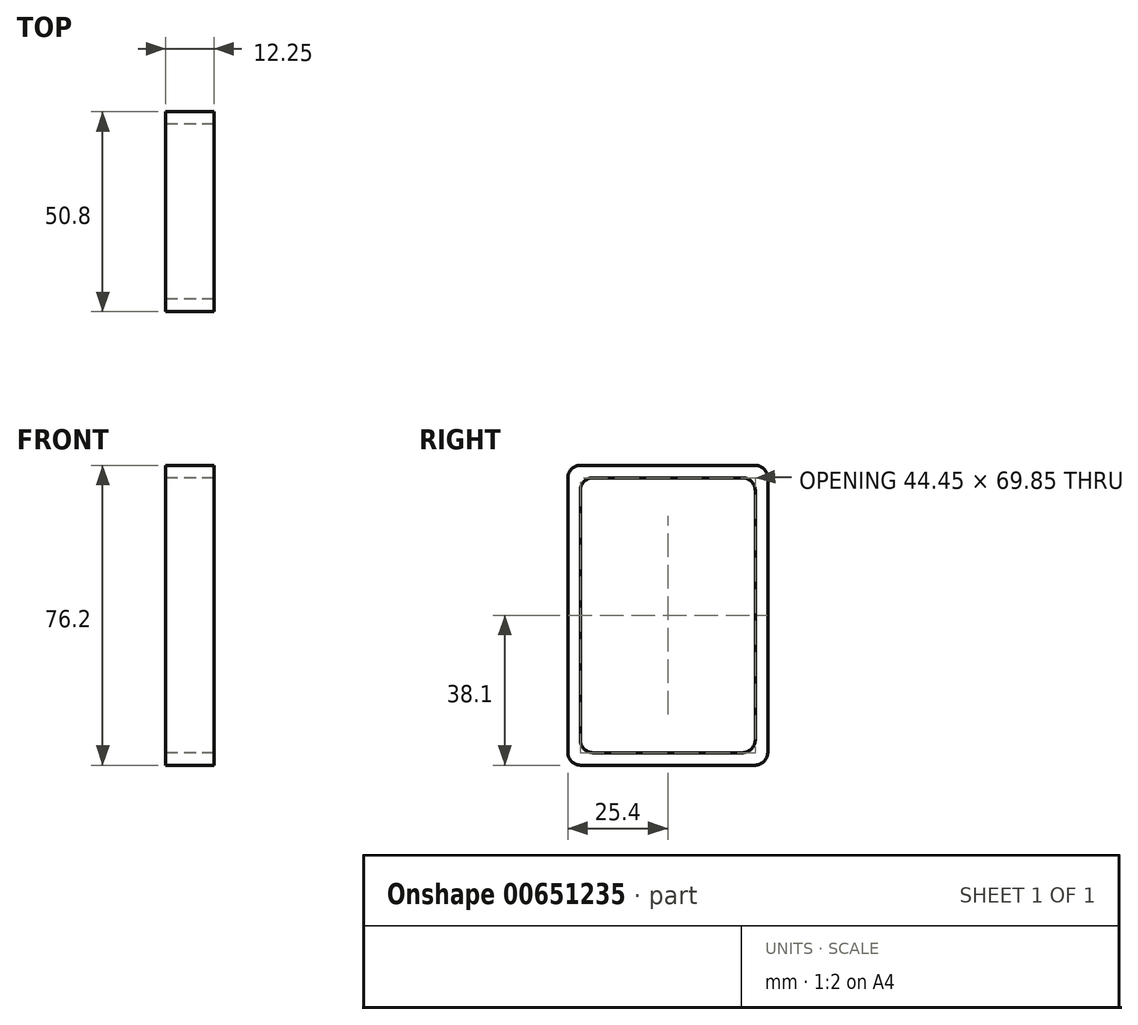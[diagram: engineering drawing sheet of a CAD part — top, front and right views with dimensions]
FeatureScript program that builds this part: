
annotation { "Feature Type Name" : "Feature", "Feature Type Description" : "" }
export const myFeature = defineFeature(function(context is Context, id is Id, definition is map)
    precondition{}
    {
        {
            var Q0;
            Q0=qCreatedBy(makeId("Right.planeOp"),FACE);
            var sketch = newSketch(context, id + "F0", { "sketchPlane" : qUnion([Q0])});
            skLineSegment(sketch, "E0.bottom", {"start": v(25.4, -38.1) * mm, "end": v(-25.4, -38.1) * mm});
            skLineSegment(sketch, "E0.top", {"start": v(25.4, 38.1) * mm, "end": v(-25.4, 38.1) * mm});
            skLineSegment(sketch, "E0.left", {"start": v(25.4, -38.1) * mm, "end": v(25.4, 38.1) * mm});
            skLineSegment(sketch, "E0.right", {"start": v(-25.4, -38.1) * mm, "end": v(-25.4, 38.1) * mm});
            skPoint(sketch, "E0.middle", {"position": v(0, 0) * mm});
            skLineSegment(sketch, "E1.bottom", {"start": v(22.22, -34.92) * mm, "end": v(-22.23, -34.93) * mm});
            skLineSegment(sketch, "E1.top", {"start": v(22.23, 34.93) * mm, "end": v(-22.23, 34.93) * mm});
            skLineSegment(sketch, "E1.left", {"start": v(22.23, -34.92) * mm, "end": v(22.23, 34.93) * mm});
            skLineSegment(sketch, "E1.right", {"start": v(-22.23, -34.93) * mm, "end": v(-22.22, 34.93) * mm});
            skSolve(sketch);
        }
        {
            assignVariable(context, id + "F1", {"name" : "Length", "anyValue" : 12.25});
        }
        {
            var Q0;
            Q0=makeQuery(id+"F0.imprint","IMPRINT",FACE,{"disambiguationData":[TD([[makeQuery(id+"F0.imprint","IMPRINT",EDGE,{"derivedFrom":sQuery(id+"F0.wireOp",EDGE,"E0.bottom")}),-1.0]])]});
            extrude(context, id + "F2", {"entities" : qUnion([Q0]), "depth" : (getVariable(context, 'Length')) * mm, "offsetDistance" : 25.4 * mm});
        }
        {
            var Q0;
            Q0=makeQuery(id+"F2.opExtrude","SWEPT_EDGE",EDGE,{"disambiguationData":[OSD([sQuery(id+"F0.wireOp",EDGE,"E0.top"),sQuery(id+"F0.wireOp",EDGE,"E0.right")])]});
            var Q1;
            Q1=makeQuery(id+"F2.opExtrude","SWEPT_EDGE",EDGE,{"disambiguationData":[OSD([sQuery(id+"F0.wireOp",EDGE,"E1.top"),sQuery(id+"F0.wireOp",EDGE,"E1.right")])]});
            var Q2;
            Q2=makeQuery(id+"F2.opExtrude","SWEPT_EDGE",EDGE,{"disambiguationData":[OSD([sQuery(id+"F0.wireOp",EDGE,"E1.top"),sQuery(id+"F0.wireOp",EDGE,"E1.left")])]});
            var Q3;
            Q3=makeQuery(id+"F2.opExtrude","SWEPT_EDGE",EDGE,{"disambiguationData":[OSD([sQuery(id+"F0.wireOp",EDGE,"E0.top"),sQuery(id+"F0.wireOp",EDGE,"E0.left")])]});
            var Q4;
            Q4=makeQuery(id+"F2.opExtrude","SWEPT_EDGE",EDGE,{"disambiguationData":[OSD([sQuery(id+"F0.wireOp",EDGE,"E0.bottom"),sQuery(id+"F0.wireOp",EDGE,"E0.left")])]});
            var Q5;
            Q5=makeQuery(id+"F2.opExtrude","SWEPT_EDGE",EDGE,{"disambiguationData":[OSD([sQuery(id+"F0.wireOp",EDGE,"E0.bottom"),sQuery(id+"F0.wireOp",EDGE,"E0.right")])]});
            var Q6;
            Q6=makeQuery(id+"F2.opExtrude","SWEPT_EDGE",EDGE,{"disambiguationData":[OSD([sQuery(id+"F0.wireOp",EDGE,"E1.bottom"),sQuery(id+"F0.wireOp",EDGE,"E1.left")])]});
            var Q7;
            Q7=makeQuery(id+"F2.opExtrude","SWEPT_EDGE",EDGE,{"disambiguationData":[OSD([sQuery(id+"F0.wireOp",EDGE,"E1.bottom"),sQuery(id+"F0.wireOp",EDGE,"E1.right")])]});
            fillet(context, id + "F3", {"entities" : qUnion([Q0, Q1, Q2, Q3, Q4, Q5, Q6, Q7]), "radius" : 3.17 * mm, "tangentPropagation" : true, "allowEdgeOverflow" : false});
        }
        {
            var Q0;
            Q0=makeQuery(id+"F2.opExtrude","SWEPT_FACE",FACE,{"disambiguationData":[OSD([sQuery(id+"F0.wireOp",EDGE,"E0.right")])]});
            var sketch = newSketch(context, id + "F4", { "sketchPlane" : qUnion([Q0])});
            skLineSegment(sketch, "E2", {"start": v(155.58, 0) * mm, "end": v(53.98, 0) * mm});
            skPoint(sketch, "E3.middle", {"position": v(53.98, 0) * mm});
            skCircle(sketch, "E4", {"center": v(69.98, 15) * mm, "radius": 3 * mm});
            skCircle(sketch, "E5", {"center": v(37.98, 15) * mm, "radius": 3 * mm});
            skCircle(sketch, "E6", {"center": v(69.98, -15) * mm, "radius": 3 * mm});
            skCircle(sketch, "E7", {"center": v(37.98, -15) * mm, "radius": 3 * mm});
            skCircle(sketch, "E8.MirrorC", {"center": v(241.18, 15) * mm, "radius": 3 * mm});
            skCircle(sketch, "E9.MirrorC", {"center": v(273.18, 15) * mm, "radius": 3 * mm});
            skCircle(sketch, "E10.MirrorC", {"center": v(273.18, -15) * mm, "radius": 3 * mm});
            skCircle(sketch, "E11.MirrorC", {"center": v(241.18, -15) * mm, "radius": 3 * mm});
            skPoint(sketch, "E12.middle", {"position": v(155.58, 0) * mm});
            skCircle(sketch, "E13", {"center": v(117.48, 12.7) * mm, "radius": 3 * mm});
            skCircle(sketch, "E14", {"center": v(193.68, 12.7) * mm, "radius": 3 * mm});
            skCircle(sketch, "E15", {"center": v(193.68, -12.7) * mm, "radius": 3 * mm});
            skCircle(sketch, "E16", {"center": v(117.48, -12.7) * mm, "radius": 3 * mm});
            skSolve(sketch);
        }
        {
            var Q0;
            Q0=makeQuery(id+"F4.imprint","IMPRINT",FACE,{"disambiguationData":[TD([[makeQuery(id+"F4.imprint","IMPRINT",EDGE,{"derivedFrom":sQuery(id+"F4.wireOp",EDGE,"E5")}),1.0]])]});
            var Q1;
            Q1=makeQuery(id+"F4.imprint","IMPRINT",FACE,{"disambiguationData":[TD([[makeQuery(id+"F4.imprint","IMPRINT",EDGE,{"derivedFrom":sQuery(id+"F4.wireOp",EDGE,"E4")}),1.0]])]});
            var Q2;
            Q2=makeQuery(id+"F4.imprint","IMPRINT",FACE,{"disambiguationData":[TD([[makeQuery(id+"F4.imprint","IMPRINT",EDGE,{"derivedFrom":sQuery(id+"F4.wireOp",EDGE,"E6")}),1.0]])]});
            var Q3;
            Q3=makeQuery(id+"F4.imprint","IMPRINT",FACE,{"disambiguationData":[TD([[makeQuery(id+"F4.imprint","IMPRINT",EDGE,{"derivedFrom":sQuery(id+"F4.wireOp",EDGE,"E7")}),1.0]])]});
            var Q4;
            Q4=makeQuery(id+"F4.imprint","IMPRINT",FACE,{"disambiguationData":[TD([[makeQuery(id+"F4.imprint","IMPRINT",EDGE,{"derivedFrom":sQuery(id+"F4.wireOp",EDGE,"E8.MirrorC")}),-1.0]])]});
            var Q5;
            Q5=makeQuery(id+"F4.imprint","IMPRINT",FACE,{"disambiguationData":[TD([[makeQuery(id+"F4.imprint","IMPRINT",EDGE,{"derivedFrom":sQuery(id+"F4.wireOp",EDGE,"E9.MirrorC")}),-1.0]])]});
            var Q6;
            Q6=makeQuery(id+"F4.imprint","IMPRINT",FACE,{"disambiguationData":[TD([[makeQuery(id+"F4.imprint","IMPRINT",EDGE,{"derivedFrom":sQuery(id+"F4.wireOp",EDGE,"E10.MirrorC")}),-1.0]])]});
            var Q7;
            Q7=makeQuery(id+"F4.imprint","IMPRINT",FACE,{"disambiguationData":[TD([[makeQuery(id+"F4.imprint","IMPRINT",EDGE,{"derivedFrom":sQuery(id+"F4.wireOp",EDGE,"E11.MirrorC")}),-1.0]])]});
            extrude(context, id + "F5", {"entities" : qUnion([Q0, Q1, Q2, Q3, Q4, Q5, Q6, Q7]), "operationType" : NewBodyOperationType.REMOVE, "oppositeDirection" : true, "depth" : 25.4 * mm, "offsetDistance" : 25.4 * mm});
        }
        {
            var Q0;
            Q0=makeQuery(id+"F4.imprint","IMPRINT",FACE,{"disambiguationData":[TD([[makeQuery(id+"F4.imprint","IMPRINT",EDGE,{"derivedFrom":sQuery(id+"F4.wireOp",EDGE,"E13")}),1.0]])]});
            var Q1;
            Q1=makeQuery(id+"F4.imprint","IMPRINT",FACE,{"disambiguationData":[TD([[makeQuery(id+"F4.imprint","IMPRINT",EDGE,{"derivedFrom":sQuery(id+"F4.wireOp",EDGE,"E16")}),1.0]])]});
            var Q2;
            Q2=makeQuery(id+"F4.imprint","IMPRINT",FACE,{"disambiguationData":[TD([[makeQuery(id+"F4.imprint","IMPRINT",EDGE,{"derivedFrom":sQuery(id+"F4.wireOp",EDGE,"E15")}),1.0]])]});
            var Q3;
            Q3=makeQuery(id+"F4.imprint","IMPRINT",FACE,{"disambiguationData":[TD([[makeQuery(id+"F4.imprint","IMPRINT",EDGE,{"derivedFrom":sQuery(id+"F4.wireOp",EDGE,"E14")}),1.0]])]});
            extrude(context, id + "F6", {"entities" : qUnion([Q0, Q1, Q2, Q3]), "operationType" : NewBodyOperationType.REMOVE, "oppositeDirection" : true, "depth" : 25.4 * mm, "offsetDistance" : 25.4 * mm});
        }
    });
